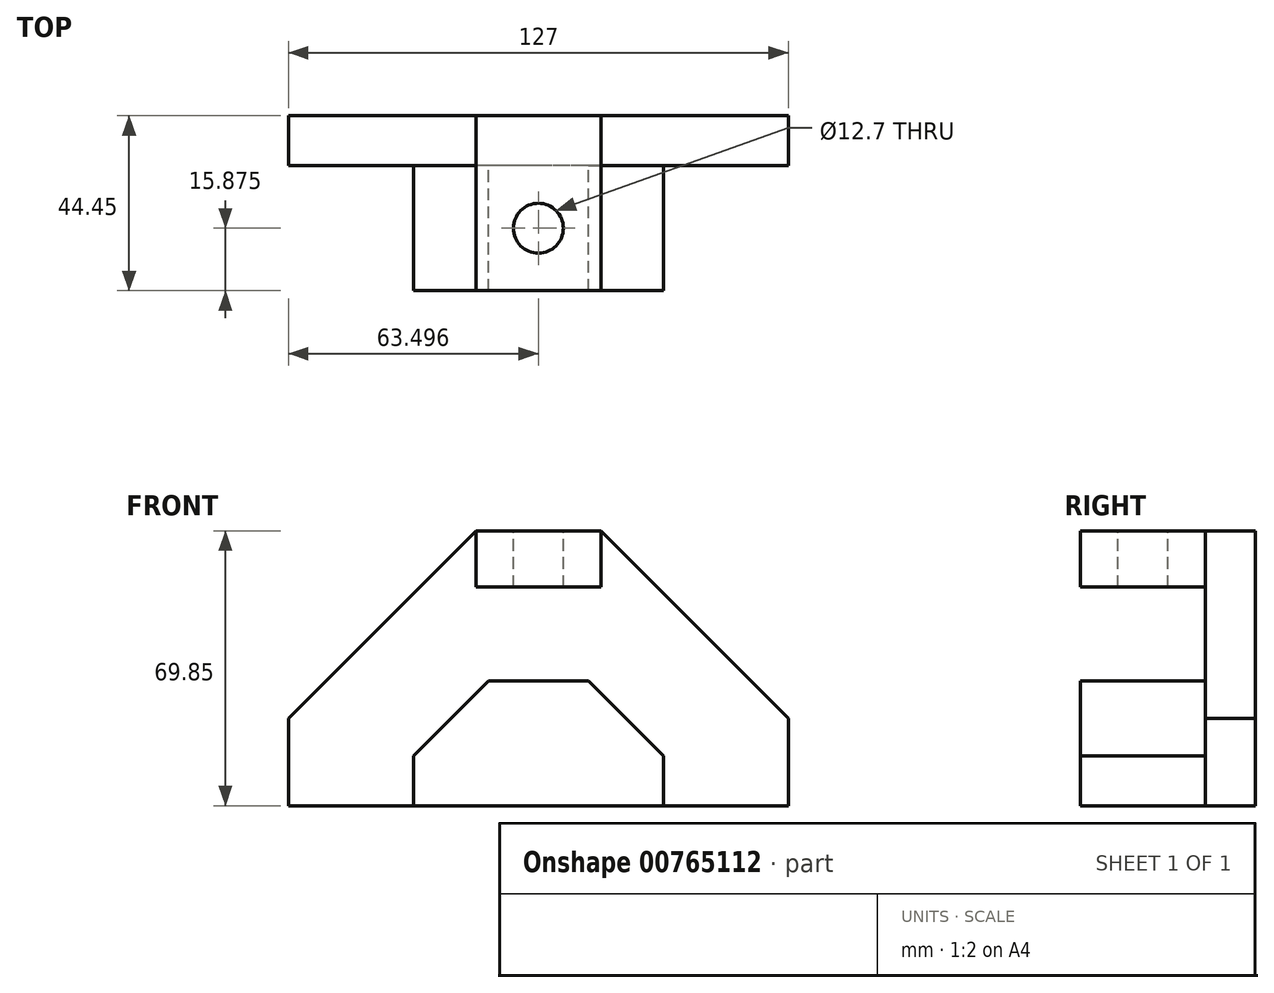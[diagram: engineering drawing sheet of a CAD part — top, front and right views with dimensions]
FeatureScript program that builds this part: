
annotation { "Feature Type Name" : "Feature", "Feature Type Description" : "" }
export const myFeature = defineFeature(function(context is Context, id is Id, definition is map)
    precondition{}
    {
        {
            var Q0;
            Q0=qCreatedBy(makeId("Front.planeOp"),FACE);
            var sketch = newSketch(context, id + "F0", { "sketchPlane" : qUnion([Q0])});
            skLineSegment(sketch, "E0", {"start": v(-57.33, -36.74) * mm, "end": v(69.67, -36.74) * mm});
            skLineSegment(sketch, "E1", {"start": v(69.67, -36.74) * mm, "end": v(69.67, -14.51) * mm});
            skLineSegment(sketch, "E2", {"start": v(22.04, 33.11) * mm, "end": v(-9.7, 33.11) * mm});
            skLineSegment(sketch, "E3", {"start": v(-57.33, -14.51) * mm, "end": v(-57.33, -36.74) * mm});
            skLineSegment(sketch, "E4", {"start": v(22.04, 33.11) * mm, "end": v(69.67, -14.51) * mm});
            skLineSegment(sketch, "E5", {"start": v(-57.33, -14.51) * mm, "end": v(-9.7, 33.11) * mm});
            skSolve(sketch);
        }
        {
            var Q0;
            Q0 = qSketchRegion(id + "F0", true);
            extrude(context, id + "F1", {"entities" : qUnion([Q0]), "depth" : 12.7 * mm, "offsetDistance" : 25.4 * mm});
        }
        {
            var Q0;
            Q0=makeQuery(id+"F1.opExtrude","CAP_FACE",FACE,{"disambiguationData":[OSD([sQuery(id+"F0.wireOp",EDGE,"E0"),sQuery(id+"F0.wireOp",EDGE,"E1"),sQuery(id+"F0.wireOp",EDGE,"E2"),sQuery(id+"F0.wireOp",EDGE,"E3"),sQuery(id+"F0.wireOp",EDGE,"E4"),sQuery(id+"F0.wireOp",EDGE,"E5")])],"isStart":false});
            var sketch = newSketch(context, id + "F2", { "sketchPlane" : qUnion([Q0])});
            skLineSegment(sketch, "E6", {"start": v(69.67, -36.74) * mm, "end": v(37.92, -36.74) * mm});
            skLineSegment(sketch, "E7", {"start": v(37.92, -36.74) * mm, "end": v(-25.58, -36.74) * mm});
            skLineSegment(sketch, "E8", {"start": v(37.92, -36.74) * mm, "end": v(37.92, -24.04) * mm});
            skLineSegment(sketch, "E9", {"start": v(-25.58, -36.74) * mm, "end": v(-25.58, -24.04) * mm});
            skLineSegment(sketch, "E10", {"start": v(-25.58, -24.04) * mm, "end": v(-6.53, -24.04) * mm});
            skLineSegment(sketch, "E11", {"start": v(37.92, -24.04) * mm, "end": v(18.87, -24.04) * mm});
            skLineSegment(sketch, "E12", {"start": v(18.87, -24.04) * mm, "end": v(18.87, -4.99) * mm});
            skLineSegment(sketch, "E13", {"start": v(18.87, -4.99) * mm, "end": v(-6.53, -4.99) * mm});
            skLineSegment(sketch, "E14", {"start": v(-6.53, -4.99) * mm, "end": v(-6.53, -24.04) * mm});
            skLineSegment(sketch, "E15", {"start": v(-6.53, -4.99) * mm, "end": v(-25.58, -24.04) * mm});
            skLineSegment(sketch, "E16", {"start": v(18.87, -4.99) * mm, "end": v(37.92, -24.04) * mm});
            skSolve(sketch);
        }
        {
            var Q0;
            Q0 = qSketchRegion(id + "F2", true);
            extrude(context, id + "F3", {"entities" : qUnion([Q0]), "operationType" : NewBodyOperationType.ADD, "depth" : 31.75 * mm, "offsetDistance" : 25.4 * mm});
        }
        {
            var Q0;
            Q0=makeQuery(id+"F1.opExtrude","CAP_FACE",FACE,{"disambiguationData":[OSD([sQuery(id+"F0.wireOp",EDGE,"E0"),sQuery(id+"F0.wireOp",EDGE,"E1"),sQuery(id+"F0.wireOp",EDGE,"E2"),sQuery(id+"F0.wireOp",EDGE,"E3"),sQuery(id+"F0.wireOp",EDGE,"E4"),sQuery(id+"F0.wireOp",EDGE,"E5")])],"isStart":false});
            var sketch = newSketch(context, id + "F4", { "sketchPlane" : qUnion([Q0])});
            skLineSegment(sketch, "E17", {"start": v(22.04, 33.11) * mm, "end": v(22.04, 18.83) * mm});
            skLineSegment(sketch, "E18", {"start": v(22.04, 18.83) * mm, "end": v(-9.7, 18.83) * mm});
            skLineSegment(sketch, "E19", {"start": v(-9.7, 18.83) * mm, "end": v(-9.7, 33.11) * mm});
            skSolve(sketch);
        }
        {
            var Q0;
            Q0 = qSketchRegion(id + "F4", true);
            var Q1;
            Q1=makeQuery(id+"F4.imprint","IMPRINT",FACE,{"disambiguationData":[TD([[makeQuery(id+"F4.imprint","IMPRINT",EDGE,{"derivedFrom":sQuery(id+"F4.wireOp",EDGE,"E17")}),-1.0]])]});
            extrude(context, id + "F5", {"entities" : qUnion([Q0, Q1]), "operationType" : NewBodyOperationType.ADD, "depth" : 31.75 * mm, "offsetDistance" : 25.4 * mm});
        }
        {
            var Q0;
            {var subQ0=sQuery(id+"F0.wireOp",EDGE,"E2");Q0=makeQuery(id+"F5.boolean.opBoolean","MERGE",FACE,{"derivedFrom":[makeQuery(id+"F1.opExtrude","SWEPT_FACE",FACE,{"disambiguationData":[OSD([subQ0])]}),makeQuery(id+"F5.opExtrude","SWEPT_FACE",FACE,{"disambiguationData":[OSD([subQ0])]})]});}
            var sketch = newSketch(context, id + "F6", { "sketchPlane" : qUnion([Q0])});
            skLineSegment(sketch, "E20", {"start": v(6.17, -44.45) * mm, "end": v(6.17, -28.58) * mm});
            skCircle(sketch, "E21", {"center": v(6.17, -28.58) * mm, "radius": 6.35 * mm});
            skSolve(sketch);
        }
        {
            var Q0;
            Q0 = qSketchRegion(id + "F6", true);
            extrude(context, id + "F7", {"entities" : qUnion([Q0]), "operationType" : NewBodyOperationType.REMOVE, "oppositeDirection" : true, "depth" : 25.4 * mm, "offsetDistance" : 25.4 * mm});
        }
    });
